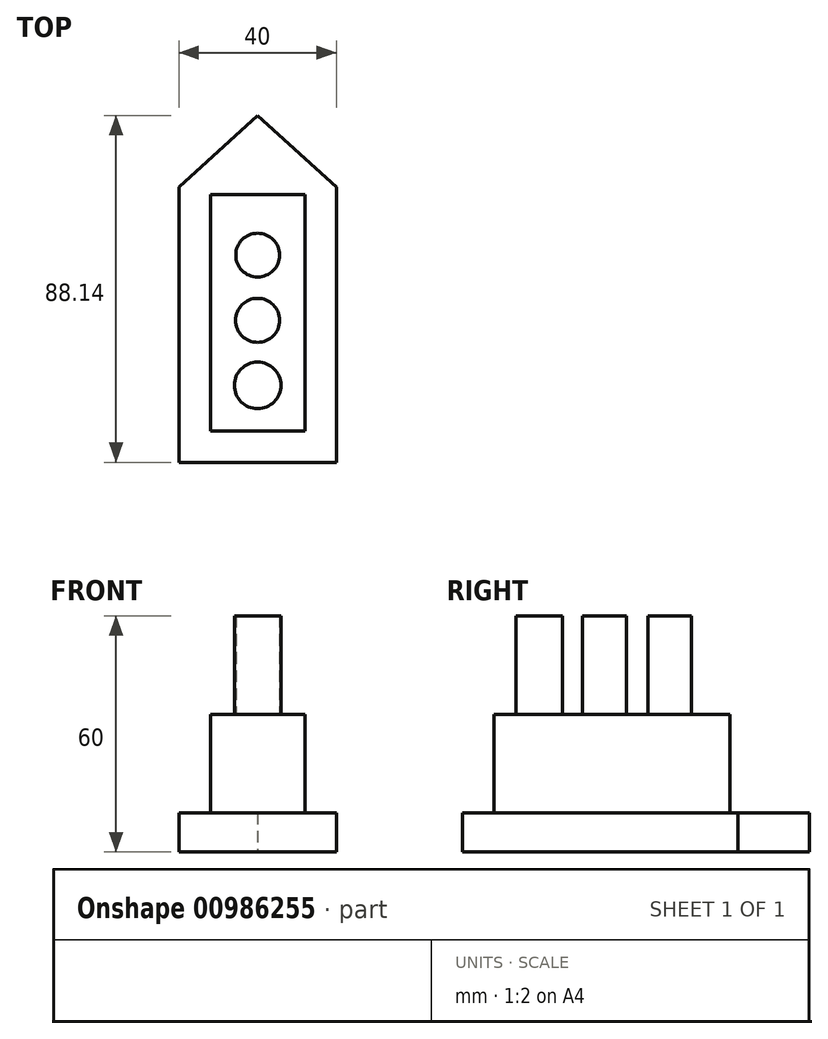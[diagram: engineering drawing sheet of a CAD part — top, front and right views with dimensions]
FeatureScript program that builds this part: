
annotation { "Feature Type Name" : "Feature", "Feature Type Description" : "" }
export const myFeature = defineFeature(function(context is Context, id is Id, definition is map)
    precondition{}
    {
        {
            var Q0;
            Q0=qCreatedBy(makeId("Top.planeOp"),FACE);
            var sketch = newSketch(context, id + "F0", { "sketchPlane" : qUnion([Q0])});
            skLineSegment(sketch, "E0", {"start": v(-20, 33.91) * mm, "end": v(-20, -36.09) * mm});
            skLineSegment(sketch, "E1", {"start": v(-20, -36.09) * mm, "end": v(20, -36.09) * mm});
            skLineSegment(sketch, "E2", {"start": v(-20, 33.91) * mm, "end": v(0, 52.05) * mm});
            skLineSegment(sketch, "E3", {"start": v(20, -36.09) * mm, "end": v(20, 33.91) * mm});
            skLineSegment(sketch, "E4", {"start": v(0, 52.05) * mm, "end": v(20, 33.91) * mm});
            skSolve(sketch);
        }
        {
            var Q0;
            Q0=makeQuery(id+"F0.imprint","IMPRINT",FACE,{"disambiguationData":[TD([[makeQuery(id+"F0.imprint","IMPRINT",EDGE,{"derivedFrom":sQuery(id+"F0.wireOp",EDGE,"E0")}),1.0]])]});
            extrude(context, id + "F1", {"entities" : qUnion([Q0]), "depth" : 10 * mm, "offsetDistance" : 25 * mm});
        }
        {
            var Q0;
            Q0=makeQuery(id+"F1.opExtrude","CAP_FACE",FACE,{"disambiguationData":[OSD([sQuery(id+"F0.wireOp",EDGE,"E0"),sQuery(id+"F0.wireOp",EDGE,"E1"),sQuery(id+"F0.wireOp",EDGE,"E2"),sQuery(id+"F0.wireOp",EDGE,"E3"),sQuery(id+"F0.wireOp",EDGE,"E4")])],"isStart":false});
            var sketch = newSketch(context, id + "F2", { "sketchPlane" : qUnion([Q0])});
            skLineSegment(sketch, "E5.bottom", {"start": v(-12, 31.91) * mm, "end": v(12, 31.91) * mm});
            skLineSegment(sketch, "E5.top", {"start": v(-12, -28.09) * mm, "end": v(12, -28.09) * mm});
            skLineSegment(sketch, "E5.left", {"start": v(-12, 31.91) * mm, "end": v(-12, -28.09) * mm});
            skLineSegment(sketch, "E5.right", {"start": v(12, 31.91) * mm, "end": v(12, -28.09) * mm});
            skSolve(sketch);
        }
        {
            var Q0;
            Q0 = qSketchRegion(id + "F2", true);
            extrude(context, id + "F3", {"entities" : qUnion([Q0]), "operationType" : NewBodyOperationType.ADD, "depth" : 25 * mm, "offsetDistance" : 25 * mm});
        }
        {
            var Q0;
            Q0=makeQuery(id+"F3.opExtrude","CAP_FACE",FACE,{"disambiguationData":[OSD([sQuery(id+"F2.wireOp",EDGE,"E5.bottom"),sQuery(id+"F2.wireOp",EDGE,"E5.top"),sQuery(id+"F2.wireOp",EDGE,"E5.left"),sQuery(id+"F2.wireOp",EDGE,"E5.right")])],"isStart":false});
            var sketch = newSketch(context, id + "F4", { "sketchPlane" : qUnion([Q0])});
            skCircle(sketch, "E6", {"center": v(0, 16.57) * mm, "radius": 5.56 * mm});
            skCircle(sketch, "E7", {"center": v(0, 0) * mm, "radius": 5.6 * mm});
            skCircle(sketch, "E8", {"center": v(0, -16.51) * mm, "radius": 5.91 * mm});
            skSolve(sketch);
        }
        {
            var Q0;
            Q0 = qSketchRegion(id + "F4", true);
            extrude(context, id + "F5", {"entities" : qUnion([Q0]), "operationType" : NewBodyOperationType.ADD, "depth" : 25 * mm, "offsetDistance" : 25 * mm});
        }
    });
